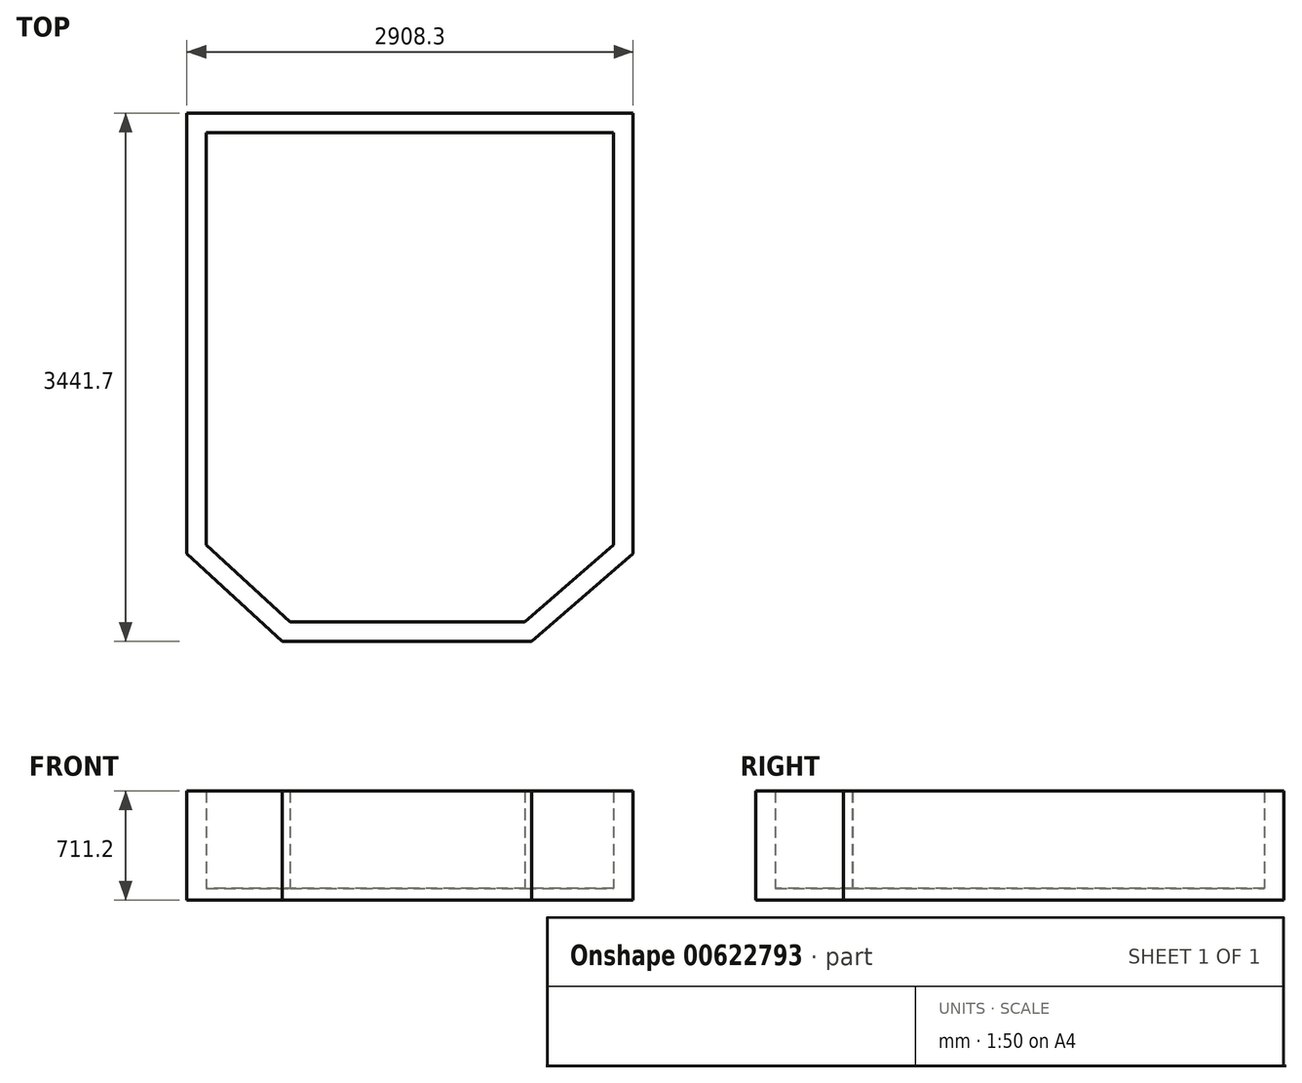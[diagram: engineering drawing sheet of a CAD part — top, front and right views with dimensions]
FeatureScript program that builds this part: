
annotation { "Feature Type Name" : "Feature", "Feature Type Description" : "" }
export const myFeature = defineFeature(function(context is Context, id is Id, definition is map)
    precondition{}
    {
        {
            var Q0;
            Q0=qCreatedBy(makeId("Top.planeOp"),FACE);
            var sketch = newSketch(context, id + "F0", { "sketchPlane" : qUnion([Q0])});
            skLineSegment(sketch, "E0", {"start": v(0, 0) * mm, "end": v(2908.3, 0) * mm});
            skLineSegment(sketch, "E1", {"start": v(2247.9, -3441.7) * mm, "end": v(622.3, -3441.7) * mm});
            skPoint(sketch, "E2.end.orphan", {"position": v(0, -2870.2) * mm});
            skLineSegment(sketch, "E3", {"start": v(622.3, -3441.7) * mm, "end": v(0, -2870.2) * mm});
            skLineSegment(sketch, "E4", {"start": v(0, -2870.2) * mm, "end": v(0, 0) * mm});
            skPoint(sketch, "E5.start.orphan", {"position": v(2870.2, -2870.2) * mm});
            skLineSegment(sketch, "E6", {"start": v(2908.3, 0) * mm, "end": v(2908.3, -2870.2) * mm});
            skLineSegment(sketch, "E7", {"start": v(2247.9, -3441.7) * mm, "end": v(2908.3, -2870.2) * mm});
            skSolve(sketch);
        }
        {
            var Q0;
            Q0 = qSketchRegion(id + "F0", true);
            extrude(context, id + "F1", {"entities" : qUnion([Q0]), "depth" : 76.2 * mm, "offsetDistance" : 25.4 * mm});
        }
        {
            var Q0;
            Q0=makeQuery(id+"F1.opExtrude","CAP_FACE",FACE,{"disambiguationData":[OSD([sQuery(id+"F0.wireOp",EDGE,"E0"),sQuery(id+"F0.wireOp",EDGE,"E1"),sQuery(id+"F0.wireOp",EDGE,"E3"),sQuery(id+"F0.wireOp",EDGE,"E4"),sQuery(id+"F0.wireOp",EDGE,"E6"),sQuery(id+"F0.wireOp",EDGE,"E7")])],"isStart":false});
            var sketch = newSketch(context, id + "F2", { "sketchPlane" : qUnion([Q0])});
            skPoint(sketch, "E8.end.orphan", {"position": v(2247.9, -3513.67) * mm});
            skLineSegment(sketch, "E9", {"start": v(0, 0) * mm, "end": v(0, -2870.2) * mm});
            skLineSegment(sketch, "E10", {"start": v(0, -2870.2) * mm, "end": v(622.3, -3441.7) * mm});
            skLineSegment(sketch, "E11", {"start": v(622.3, -3441.7) * mm, "end": v(2247.9, -3441.7) * mm});
            skLineSegment(sketch, "E12", {"start": v(2247.9, -3441.7) * mm, "end": v(2908.3, -2870.2) * mm});
            skLineSegment(sketch, "E13", {"start": v(2908.3, 0) * mm, "end": v(2908.3, -2870.2) * mm});
            skLineSegment(sketch, "E14", {"start": v(0, 0) * mm, "end": v(2908.3, 0) * mm});
            skLineSegment(sketch, "E15.0", {"start": v(2901.95, 0) * mm, "end": v(2901.95, -2870.2) * mm});
            skLineSegment(sketch, "E16.0", {"start": v(127, -127) * mm, "end": v(127, -2814.4) * mm});
            skLineSegment(sketch, "E16.1", {"start": v(671.77, -3314.7) * mm, "end": v(2200.58, -3314.7) * mm});
            skLineSegment(sketch, "E16.2", {"start": v(2200.58, -3314.7) * mm, "end": v(2781.3, -2812.15) * mm});
            skLineSegment(sketch, "E16.3", {"start": v(127, -2814.4) * mm, "end": v(671.77, -3314.7) * mm});
            skLineSegment(sketch, "E16.4", {"start": v(2781.3, -2812.15) * mm, "end": v(2781.3, -127) * mm});
            skLineSegment(sketch, "E16.5", {"start": v(2781.3, -127) * mm, "end": v(127, -127) * mm});
            skSolve(sketch);
        }
        {
            var Q0;
            Q0 = qSketchRegion(id + "F2", true);
            extrude(context, id + "F3", {"entities" : qUnion([Q0]), "operationType" : NewBodyOperationType.ADD, "depth" : 635 * mm, "offsetDistance" : 25.4 * mm});
        }
    });
